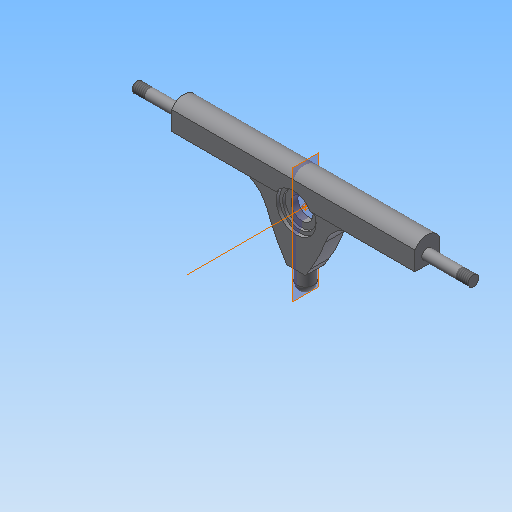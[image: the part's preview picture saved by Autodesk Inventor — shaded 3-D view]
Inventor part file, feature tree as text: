
AUTODESK INVENTOR PART (.ipt)
format: ipt  version: 2017 (Build 210142000, 142)  size: 205,312 bytes
history: native  units: in
note: dims shown in document units (in); Inventor stores cm internally (conversion verified against a paired STEP export)
features: extrude x7, plane x6, sketch x5, fillet x4, mirror x2, thread x2, other x2
ambient origin geometry x8: Origin, YZ Plane, XZ Plane, XY Plane, X Axis, Y Axis, Z Axis, Center Point
bodies: Solid1 (feature_tree)
feature tree (28):
  extrude  "Truck Axle"  Depth=0.72in
  extrude  "Axle"  Depth=1.375in TaperAngle=0.0deg
  plane  "Work Plane1"
  mirror  "Other Axle"
  plane  "Work Plane3"
  extrude  "Pentagon"  Depth=1.0in
  fillet  "Fillet1"  Radius=1.0in
  sketch  "Sketch6"  dims[d31=2.0in d32=0.0in d37=0.65in d38=0.0in]
  extrude  "Inner hole"  Depth=0.65in TaperAngle=0.0deg
  extrude  "Middle hole"  Depth=0.41in
  extrude  "Outer hole"  Depth=0.41in TaperAngle=0.0deg
  extrude  "Ball joint"  Depth=0.41in TaperAngle=0.0deg
  fillet  "Fillet3"  Radius=0.5in
  thread  "Thread3"  [1 undecoded]
  thread  "Thread4"  [1 undecoded]
  fillet  "Fillet6"  Radius=5.0in
  plane  "Work Plane4"
  mirror  "Mirror2"
  fillet  "Fillet7"  Radius=0.65in
  other  "Work Point1"
  plane  "Work Plane6"
  sketch  "Sketch1"  dims[d0=0.56in d1=0.72in]
  sketch  "Sketch2"  dims[d6=7.2047in d7=0.0in d8=1.375in d9=0.0in]
  plane  "Work Plane2"
  sketch  "Sketch4"  dims[d19=0.5512in d20=0.0in d25=0.55in d29=1.0in]
  sketch  "Sketch10"  dims[d39=0.05in d40=0.3125in d41=0.375in d42=0.0in d43=0.375in d44=0.0in d45=0.5in d49=1.8in d50=1.6in d53=5.0in d54=0.65in d56=1.0in d57=1.1811in d58=1.0in d59=0.0in d60=0.1772in d61=0.0in d62=1.0in d63=0.0984in d64=0.0in d65=0.0in d67=1.4961in d68=0.25in d70=1.0in d72=0.41in]
  other  "Work Axis1"
  plane  "Work Plane5"
note: 2 required parameter values undecoded (feature->parameter linkage not recoverable at this tier; creation-order binding heuristic only, values carry confidence <= 0.55)
